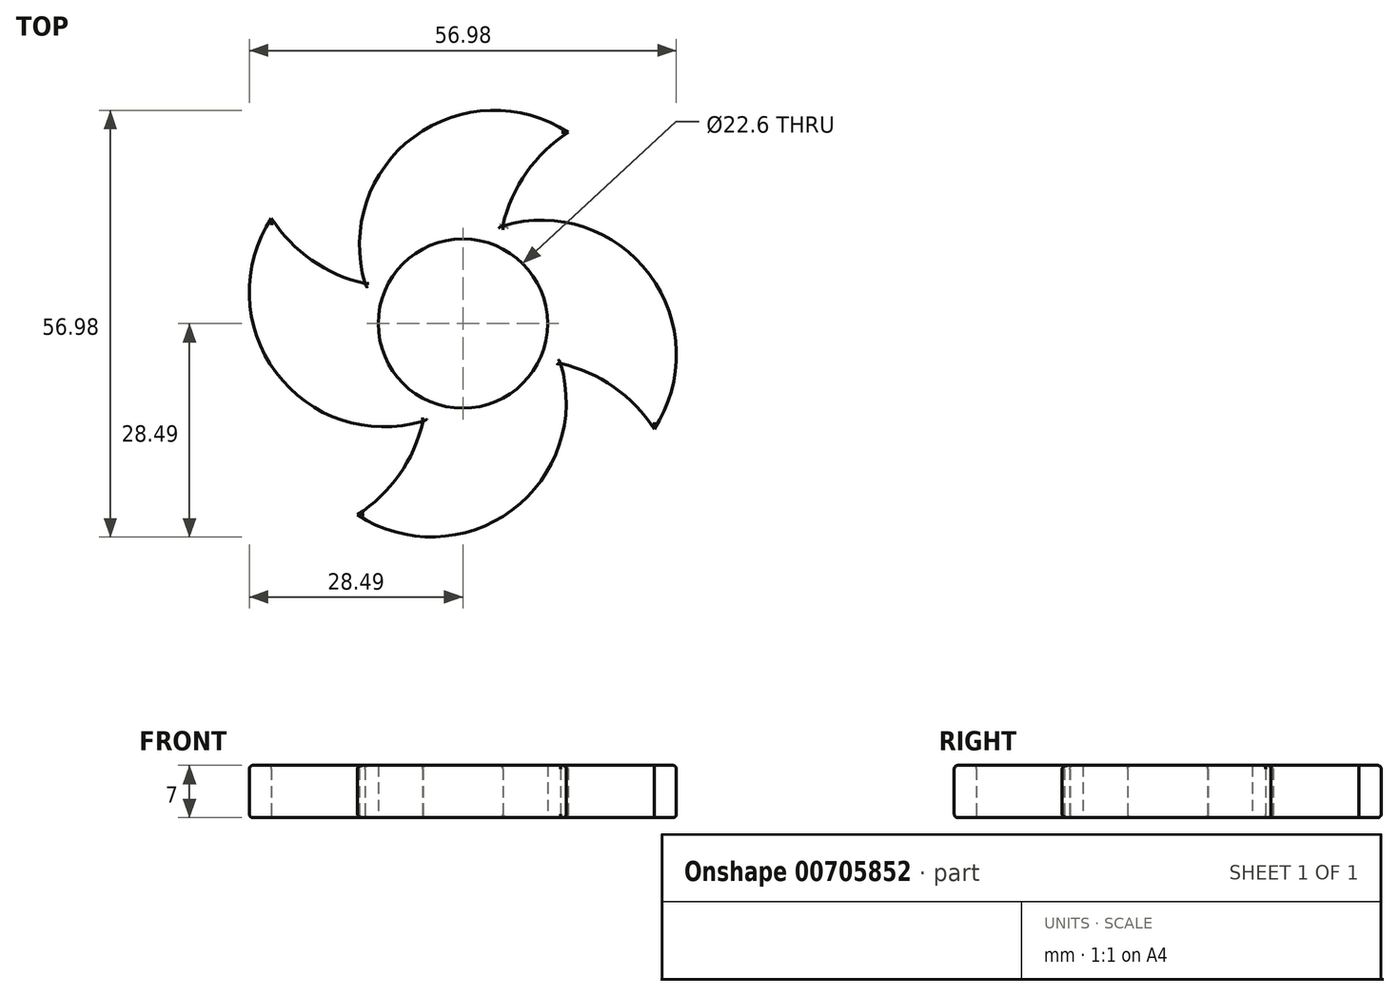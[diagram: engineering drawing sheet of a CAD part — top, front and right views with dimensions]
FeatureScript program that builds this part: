
annotation { "Feature Type Name" : "Feature", "Feature Type Description" : "" }
export const myFeature = defineFeature(function(context is Context, id is Id, definition is map)
    precondition{}
    {
        {
            var Q0;
            Q0=qCreatedBy(makeId("Top.planeOp"),FACE);
            var sketch = newSketch(context, id + "F0", { "sketchPlane" : qUnion([Q0])});
            skCircle(sketch, "E0", {"center": v(0, 0) * mm, "radius": 11.3 * mm});
            skCircle(sketch, "E1", {"center": v(0, 0) * mm, "radius": 14.12 * mm});
            skCircle(sketch, "E2", {"center": v(4.2, 10.5) * mm, "radius": 18 * mm});
            skCircle(sketch, "E3", {"center": v(24.85, 8.68) * mm, "radius": 20 * mm});
            skSolve(sketch);
        }
        {
            var Q0;
            {var subQ0=sQuery(id+"F0.wireOp",EDGE,"Av277wgP-tCuC-d8GK-UjtS-Sbt9RmJKMMHR");var subQ1=sQuery(id+"F0.wireOp",EDGE,"E1");var subQ2=makeQuery(id+"F0.imprint","INTERSECT",VERTEX,{"disambiguationData":[OD(0.0)],"derivedFrom":[subQ1,subQ0]});Q0=makeQuery(id+"F0.imprint","IMPRINT",FACE,{"disambiguationData":[TD([[makeQuery(id+"F0.imprint","IMPRINT",EDGE,{"disambiguationData":[TD([[subQ2,1.0]])],"derivedFrom":subQ1}),-1.0]])]});}
            var Q1;
            {var subQ0=sQuery(id+"F0.wireOp",EDGE,"Av277wgP-tCuC-d8GK-UjtS-Sbt9RmJKMMHR");var subQ1=sQuery(id+"F0.wireOp",EDGE,"E0");var subQ2=makeQuery(id+"F0.imprint","INTERSECT",VERTEX,{"disambiguationData":[OD(0.0)],"derivedFrom":[subQ1,subQ0]});Q1=makeQuery(id+"F0.imprint","IMPRINT",FACE,{"disambiguationData":[TD([[makeQuery(id+"F0.imprint","IMPRINT",EDGE,{"disambiguationData":[TD([[subQ2,-1.0]])],"derivedFrom":subQ1}),-1.0]])]});}
            var Q2;
            {var subQ0=sQuery(id+"F0.wireOp",EDGE,"Av277wgP-tCuC-d8GK-UjtS-Sbt9RmJKMMHR");var subQ1=sQuery(id+"F0.wireOp",EDGE,"E0");var subQ2=makeQuery(id+"F0.imprint","INTERSECT",VERTEX,{"disambiguationData":[OD(0.0)],"derivedFrom":[subQ1,subQ0]});Q2=makeQuery(id+"F0.imprint","IMPRINT",FACE,{"disambiguationData":[TD([[makeQuery(id+"F0.imprint","IMPRINT",EDGE,{"disambiguationData":[TD([[subQ2,1.0]])],"derivedFrom":subQ1}),-1.0]])]});}
            var Q3;
            {var subQ0=sQuery(id+"F0.wireOp",EDGE,"Av277wgP-tCuC-d8GK-UjtS-Sbt9RmJKMMHR");var subQ1=sQuery(id+"F0.wireOp",EDGE,"E0");var subQ2=makeQuery(id+"F0.imprint","INTERSECT",VERTEX,{"disambiguationData":[OD(1.0)],"derivedFrom":[subQ1,subQ0]});Q3=makeQuery(id+"F0.imprint","IMPRINT",FACE,{"disambiguationData":[TD([[makeQuery(id+"F0.imprint","IMPRINT",EDGE,{"disambiguationData":[TD([[subQ2,-1.0]])],"derivedFrom":subQ1}),-1.0]])]});}
            var Q4;
            {var subQ0=sQuery(id+"F0.wireOp",EDGE,"PTWYkS2m-cTii-Y78z-SZDI-GlTgDLrhLzSe");var subQ1=sQuery(id+"F0.wireOp",EDGE,"E0");var subQ2=makeQuery(id+"F0.imprint","INTERSECT",VERTEX,{"disambiguationData":[OD(0.0)],"derivedFrom":[subQ1,subQ0]});Q4=makeQuery(id+"F0.imprint","IMPRINT",FACE,{"disambiguationData":[TD([[makeQuery(id+"F0.imprint","IMPRINT",EDGE,{"disambiguationData":[TD([[subQ2,1.0]])],"derivedFrom":subQ1}),-1.0]])]});}
            var Q5;
            {var subQ0=sQuery(id+"F0.wireOp",EDGE,"LCob7wps-anE8-Zlfb-Umos-Snj1Pk7dvuzU");var subQ1=sQuery(id+"F0.wireOp",EDGE,"E0");var subQ2=makeQuery(id+"F0.imprint","INTERSECT",VERTEX,{"disambiguationData":[OD(0.0)],"derivedFrom":[subQ1,subQ0]});Q5=makeQuery(id+"F0.imprint","IMPRINT",FACE,{"disambiguationData":[TD([[makeQuery(id+"F0.imprint","IMPRINT",EDGE,{"disambiguationData":[TD([[subQ2,1.0]])],"derivedFrom":subQ1}),-1.0]])]});}
            var Q6;
            {var subQ0=sQuery(id+"F0.wireOp",EDGE,"LCob7wps-anE8-Zlfb-Umos-Snj1Pk7dvuzU");var subQ1=sQuery(id+"F0.wireOp",EDGE,"E0");var subQ2=makeQuery(id+"F0.imprint","INTERSECT",VERTEX,{"disambiguationData":[OD(0.0)],"derivedFrom":[subQ1,subQ0]});Q6=makeQuery(id+"F0.imprint","IMPRINT",FACE,{"disambiguationData":[TD([[makeQuery(id+"F0.imprint","IMPRINT",EDGE,{"disambiguationData":[TD([[subQ2,-1.0]])],"derivedFrom":subQ1}),-1.0]])]});}
            var Q7;
            {var subQ0=sQuery(id+"F0.wireOp",EDGE,"E2");var subQ1=sQuery(id+"F0.wireOp",EDGE,"E0");var subQ2=makeQuery(id+"F0.imprint","INTERSECT",VERTEX,{"disambiguationData":[OD(0.0)],"derivedFrom":[subQ1,subQ0]});Q7=makeQuery(id+"F0.imprint","IMPRINT",FACE,{"disambiguationData":[TD([[makeQuery(id+"F0.imprint","IMPRINT",EDGE,{"disambiguationData":[TD([[subQ2,-1.0]])],"derivedFrom":subQ1}),-1.0]])]});}
            var Q8;
            {var subQ0=sQuery(id+"F0.wireOp",EDGE,"LCob7wps-anE8-Zlfb-Umos-Snj1Pk7dvuzU");var subQ1=sQuery(id+"F0.wireOp",EDGE,"E0");var subQ2=makeQuery(id+"F0.imprint","INTERSECT",VERTEX,{"disambiguationData":[OD(1.0)],"derivedFrom":[subQ1,subQ0]});Q8=makeQuery(id+"F0.imprint","IMPRINT",FACE,{"disambiguationData":[TD([[makeQuery(id+"F0.imprint","IMPRINT",EDGE,{"disambiguationData":[TD([[subQ2,1.0]])],"derivedFrom":subQ1}),-1.0]])]});}
            var Q9;
            {var subQ0=sQuery(id+"F0.wireOp",EDGE,"E2");var subQ1=sQuery(id+"F0.wireOp",EDGE,"E1");var subQ2=makeQuery(id+"F0.imprint","INTERSECT",VERTEX,{"disambiguationData":[OD(0.0)],"derivedFrom":[subQ1,subQ0]});Q9=makeQuery(id+"F0.imprint","IMPRINT",FACE,{"disambiguationData":[TD([[makeQuery(id+"F0.imprint","IMPRINT",EDGE,{"disambiguationData":[TD([[subQ2,1.0]])],"derivedFrom":subQ1}),-1.0]])]});}
            var Q10;
            {var subQ0=sQuery(id+"F0.wireOp",EDGE,"E2");var subQ1=sQuery(id+"F0.wireOp",EDGE,"E0");var subQ2=makeQuery(id+"F0.imprint","INTERSECT",VERTEX,{"disambiguationData":[OD(0.0)],"derivedFrom":[subQ1,subQ0]});Q10=makeQuery(id+"F0.imprint","IMPRINT",FACE,{"disambiguationData":[TD([[makeQuery(id+"F0.imprint","IMPRINT",EDGE,{"disambiguationData":[TD([[subQ2,1.0]])],"derivedFrom":subQ1}),-1.0]])]});}
            var Q11;
            {var subQ0=sQuery(id+"F0.wireOp",EDGE,"E3");var subQ1=sQuery(id+"F0.wireOp",EDGE,"E0");var subQ2=makeQuery(id+"F0.imprint","INTERSECT",VERTEX,{"disambiguationData":[OD(0.0)],"derivedFrom":[subQ1,subQ0]});Q11=makeQuery(id+"F0.imprint","IMPRINT",FACE,{"disambiguationData":[TD([[makeQuery(id+"F0.imprint","IMPRINT",EDGE,{"disambiguationData":[TD([[subQ2,1.0]])],"derivedFrom":subQ1}),-1.0]])]});}
            var Q12;
            {var subQ0=sQuery(id+"F0.wireOp",EDGE,"E3");var subQ1=sQuery(id+"F0.wireOp",EDGE,"E0");var subQ2=makeQuery(id+"F0.imprint","INTERSECT",VERTEX,{"disambiguationData":[OD(1.0)],"derivedFrom":[subQ1,subQ0]});Q12=makeQuery(id+"F0.imprint","IMPRINT",FACE,{"disambiguationData":[TD([[makeQuery(id+"F0.imprint","IMPRINT",EDGE,{"disambiguationData":[TD([[subQ2,-1.0]])],"derivedFrom":subQ1}),-1.0]])]});}
            var Q13;
            {var subQ0=sQuery(id+"F0.wireOp",EDGE,"E3");var subQ1=sQuery(id+"F0.wireOp",EDGE,"E1");var subQ2=makeQuery(id+"F0.imprint","INTERSECT",VERTEX,{"disambiguationData":[OD(0.0)],"derivedFrom":[subQ1,subQ0]});Q13=makeQuery(id+"F0.imprint","IMPRINT",FACE,{"disambiguationData":[TD([[makeQuery(id+"F0.imprint","IMPRINT",EDGE,{"disambiguationData":[TD([[subQ2,-1.0]])],"derivedFrom":subQ1}),1.0]])]});}
            extrude(context, id + "F1", {"entities" : qUnion([Q0, Q1, Q2, Q3, Q4, Q5, Q6, Q7, Q8, Q9, Q10, Q11, Q12, Q13]), "endBound" : BoundingType.SYMMETRIC, "depth" : 7 * mm, "offsetDistance" : 25 * mm});
        }
        {
            var Q0;
            Q0=makeQuery(id+"F1.opExtrude","SWEPT_BODY",BODY,{"disambiguationData":[OSD([sQuery(id+"F0.wireOp",EDGE,"E0"),sQuery(id+"F0.wireOp",EDGE,"E1"),sQuery(id+"F0.wireOp",EDGE,"E2"),sQuery(id+"F0.wireOp",EDGE,"E3")])]});
            var Q1;
            Q1=makeQuery(id+"F1.opExtrude","SWEPT_FACE",FACE,{"disambiguationData":[OSD([sQuery(id+"F0.wireOp",EDGE,"E1")])]});
            circularPattern(context, id + "F2", {"entities" : qUnion([Q0]), "axis" : qUnion([Q1]), "angle" : 360 * degree, "instanceCount" : 4, "equalSpace" : true});
        }
        {
            var Q0;
            Q0=makeQuery(id+"F2.opPattern","COPY",BODY,{"derivedFrom":makeQuery(id+"F1.opExtrude","SWEPT_BODY",BODY,{"disambiguationData":[OSD([sQuery(id+"F0.wireOp",EDGE,"E0"),sQuery(id+"F0.wireOp",EDGE,"E1"),sQuery(id+"F0.wireOp",EDGE,"E2"),sQuery(id+"F0.wireOp",EDGE,"E3")])]}),"instanceName":"3"});
            var Q1;
            Q1=makeQuery(id+"F1.opExtrude","SWEPT_BODY",BODY,{"disambiguationData":[OSD([sQuery(id+"F0.wireOp",EDGE,"E0"),sQuery(id+"F0.wireOp",EDGE,"E1"),sQuery(id+"F0.wireOp",EDGE,"E2"),sQuery(id+"F0.wireOp",EDGE,"E3")])]});
            var Q2;
            Q2=makeQuery(id+"F2.opPattern","COPY",BODY,{"derivedFrom":makeQuery(id+"F1.opExtrude","SWEPT_BODY",BODY,{"disambiguationData":[OSD([sQuery(id+"F0.wireOp",EDGE,"E0"),sQuery(id+"F0.wireOp",EDGE,"E1"),sQuery(id+"F0.wireOp",EDGE,"E2"),sQuery(id+"F0.wireOp",EDGE,"E3")])]}),"instanceName":"1"});
            var Q3;
            Q3=makeQuery(id+"F2.opPattern","COPY",BODY,{"derivedFrom":makeQuery(id+"F1.opExtrude","SWEPT_BODY",BODY,{"disambiguationData":[OSD([sQuery(id+"F0.wireOp",EDGE,"E0"),sQuery(id+"F0.wireOp",EDGE,"E1"),sQuery(id+"F0.wireOp",EDGE,"E2"),sQuery(id+"F0.wireOp",EDGE,"E3")])]}),"instanceName":"2"});
            booleanBodies(context, id + "F3", {"operationType" : BooleanOperationType.UNION, "tools" : qUnion([Q0, Q1, Q2, Q3])});
        }
        {
            var Q0;
            Q0=makeQuery(id+"F2.opPattern","COPY",EDGE,{"derivedFrom":makeQuery(id+"F1.opExtrude","CAP_EDGE",EDGE,{"disambiguationData":[OSD([sQuery(id+"F0.wireOp",EDGE,"E3")])],"isStart":false}),"instanceName":"1"});
            var Q1;
            Q1=makeQuery(id+"F2.opPattern","COPY",EDGE,{"derivedFrom":makeQuery(id+"F1.opExtrude","CAP_EDGE",EDGE,{"disambiguationData":[OSD([sQuery(id+"F0.wireOp",EDGE,"E3")])],"isStart":true}),"instanceName":"1"});
            var Q2;
            Q2=makeQuery(id+"F2.opPattern","COPY",EDGE,{"derivedFrom":makeQuery(id+"F1.opExtrude","CAP_EDGE",EDGE,{"disambiguationData":[OSD([sQuery(id+"F0.wireOp",EDGE,"E3")])],"isStart":true}),"instanceName":"2"});
            var Q3;
            Q3=makeQuery(id+"F2.opPattern","COPY",EDGE,{"derivedFrom":makeQuery(id+"F1.opExtrude","CAP_EDGE",EDGE,{"disambiguationData":[OSD([sQuery(id+"F0.wireOp",EDGE,"E3")])],"isStart":false}),"instanceName":"2"});
            var Q4;
            Q4=makeQuery(id+"F2.opPattern","COPY",EDGE,{"derivedFrom":makeQuery(id+"F1.opExtrude","CAP_EDGE",EDGE,{"disambiguationData":[OSD([sQuery(id+"F0.wireOp",EDGE,"E3")])],"isStart":false}),"instanceName":"3"});
            var Q5;
            Q5=makeQuery(id+"F2.opPattern","COPY",EDGE,{"derivedFrom":makeQuery(id+"F1.opExtrude","CAP_EDGE",EDGE,{"disambiguationData":[OSD([sQuery(id+"F0.wireOp",EDGE,"E3")])],"isStart":true}),"instanceName":"3"});
            var Q6;
            Q6=makeQuery(id+"F1.opExtrude","CAP_EDGE",EDGE,{"disambiguationData":[OSD([sQuery(id+"F0.wireOp",EDGE,"E3")])],"isStart":false});
            var Q7;
            Q7=makeQuery(id+"F1.opExtrude","CAP_EDGE",EDGE,{"disambiguationData":[OSD([sQuery(id+"F0.wireOp",EDGE,"E3")])],"isStart":true});
            var Q8;
            Q8=makeQuery(id+"F2.opPattern","COPY",EDGE,{"derivedFrom":makeQuery(id+"F1.opExtrude","CAP_EDGE",EDGE,{"disambiguationData":[OSD([sQuery(id+"F0.wireOp",EDGE,"E2")])],"isStart":true}),"instanceName":"1"});
            var Q9;
            Q9=makeQuery(id+"F1.opExtrude","CAP_EDGE",EDGE,{"disambiguationData":[OSD([sQuery(id+"F0.wireOp",EDGE,"E2")])],"isStart":true});
            var Q10;
            Q10=makeQuery(id+"F1.opExtrude","CAP_EDGE",EDGE,{"disambiguationData":[OSD([sQuery(id+"F0.wireOp",EDGE,"E2")])],"isStart":false});
            var Q11;
            Q11=makeQuery(id+"F2.opPattern","COPY",EDGE,{"derivedFrom":makeQuery(id+"F1.opExtrude","CAP_EDGE",EDGE,{"disambiguationData":[OSD([sQuery(id+"F0.wireOp",EDGE,"E2")])],"isStart":false}),"instanceName":"1"});
            var Q12;
            Q12=makeQuery(id+"F2.opPattern","COPY",EDGE,{"derivedFrom":makeQuery(id+"F1.opExtrude","CAP_EDGE",EDGE,{"disambiguationData":[OSD([sQuery(id+"F0.wireOp",EDGE,"E2")])],"isStart":true}),"instanceName":"3"});
            var Q13;
            Q13=makeQuery(id+"F2.opPattern","COPY",EDGE,{"derivedFrom":makeQuery(id+"F1.opExtrude","CAP_EDGE",EDGE,{"disambiguationData":[OSD([sQuery(id+"F0.wireOp",EDGE,"E2")])],"isStart":false}),"instanceName":"3"});
            var Q14;
            Q14=makeQuery(id+"F2.opPattern","COPY",EDGE,{"derivedFrom":makeQuery(id+"F1.opExtrude","CAP_EDGE",EDGE,{"disambiguationData":[OSD([sQuery(id+"F0.wireOp",EDGE,"E2")])],"isStart":true}),"instanceName":"2"});
            var Q15;
            Q15=makeQuery(id+"F2.opPattern","COPY",EDGE,{"derivedFrom":makeQuery(id+"F1.opExtrude","CAP_EDGE",EDGE,{"disambiguationData":[OSD([sQuery(id+"F0.wireOp",EDGE,"E2")])],"isStart":false}),"instanceName":"2"});
            var Q16;
            {var subQ1=sQuery(id+"F0.wireOp",EDGE,"E2");var subQ2=sQuery(id+"F0.wireOp",EDGE,"E1");Q16=makeQuery(id+"F3.opBoolean","SPLIT",EDGE,{"disambiguationData":[TD([makeQuery(id+"F1.opExtrude","SWEPT_FACE",FACE,{"disambiguationData":[OSD([subQ1])]})])],"derivedFrom":makeQuery(id+"F2.opPattern","COPY",EDGE,{"derivedFrom":makeQuery(id+"F1.opExtrude","CAP_EDGE",EDGE,{"disambiguationData":[OSD([subQ2])],"isStart":false}),"instanceName":"3"})});}
            var Q17;
            {var subQ1=sQuery(id+"F0.wireOp",EDGE,"E2");var subQ2=sQuery(id+"F0.wireOp",EDGE,"E1");Q17=makeQuery(id+"F3.opBoolean","SPLIT",EDGE,{"disambiguationData":[TD([makeQuery(id+"F1.opExtrude","SWEPT_FACE",FACE,{"disambiguationData":[OSD([subQ1])]})])],"derivedFrom":makeQuery(id+"F2.opPattern","COPY",EDGE,{"derivedFrom":makeQuery(id+"F1.opExtrude","CAP_EDGE",EDGE,{"disambiguationData":[OSD([subQ2])],"isStart":true}),"instanceName":"3"})});}
            var Q18;
            {var subQ0=sQuery(id+"F0.wireOp",EDGE,"E3");var subQ2=sQuery(id+"F0.wireOp",EDGE,"E1");Q18=makeQuery(id+"F3.opBoolean","SPLIT",EDGE,{"disambiguationData":[TD([makeQuery(id+"F1.opExtrude","SWEPT_FACE",FACE,{"disambiguationData":[OSD([subQ0])]})])],"derivedFrom":makeQuery(id+"F2.opPattern","COPY",EDGE,{"derivedFrom":makeQuery(id+"F1.opExtrude","CAP_EDGE",EDGE,{"disambiguationData":[OSD([subQ2])],"isStart":false}),"instanceName":"3"})});}
            var Q19;
            {var subQ0=sQuery(id+"F0.wireOp",EDGE,"E3");var subQ2=sQuery(id+"F0.wireOp",EDGE,"E1");Q19=makeQuery(id+"F3.opBoolean","SPLIT",EDGE,{"disambiguationData":[TD([makeQuery(id+"F2.opPattern","COPY",FACE,{"derivedFrom":makeQuery(id+"F1.opExtrude","SWEPT_FACE",FACE,{"disambiguationData":[OSD([subQ0])]}),"instanceName":"1"})])],"derivedFrom":makeQuery(id+"F2.opPattern","COPY",EDGE,{"derivedFrom":makeQuery(id+"F1.opExtrude","CAP_EDGE",EDGE,{"disambiguationData":[OSD([subQ2])],"isStart":true}),"instanceName":"3"})});}
            var Q20;
            {var subQ0=sQuery(id+"F0.wireOp",EDGE,"E3");var subQ2=sQuery(id+"F0.wireOp",EDGE,"E1");Q20=makeQuery(id+"F3.opBoolean","SPLIT",EDGE,{"disambiguationData":[TD([makeQuery(id+"F2.opPattern","COPY",FACE,{"derivedFrom":makeQuery(id+"F1.opExtrude","SWEPT_FACE",FACE,{"disambiguationData":[OSD([subQ0])]}),"instanceName":"2"})])],"derivedFrom":makeQuery(id+"F2.opPattern","COPY",EDGE,{"derivedFrom":makeQuery(id+"F1.opExtrude","CAP_EDGE",EDGE,{"disambiguationData":[OSD([subQ2])],"isStart":true}),"instanceName":"3"})});}
            var Q21;
            {var subQ0=sQuery(id+"F0.wireOp",EDGE,"E3");var subQ2=sQuery(id+"F0.wireOp",EDGE,"E1");Q21=makeQuery(id+"F3.opBoolean","SPLIT",EDGE,{"disambiguationData":[TD([makeQuery(id+"F2.opPattern","COPY",FACE,{"derivedFrom":makeQuery(id+"F1.opExtrude","SWEPT_FACE",FACE,{"disambiguationData":[OSD([subQ0])]}),"instanceName":"2"})])],"derivedFrom":makeQuery(id+"F2.opPattern","COPY",EDGE,{"derivedFrom":makeQuery(id+"F1.opExtrude","CAP_EDGE",EDGE,{"disambiguationData":[OSD([subQ2])],"isStart":false}),"instanceName":"3"})});}
            var Q22;
            {var subQ0=sQuery(id+"F0.wireOp",EDGE,"E3");var subQ2=sQuery(id+"F0.wireOp",EDGE,"E1");Q22=makeQuery(id+"F3.opBoolean","SPLIT",EDGE,{"disambiguationData":[TD([makeQuery(id+"F2.opPattern","COPY",FACE,{"derivedFrom":makeQuery(id+"F1.opExtrude","SWEPT_FACE",FACE,{"disambiguationData":[OSD([subQ0])]}),"instanceName":"1"})])],"derivedFrom":makeQuery(id+"F2.opPattern","COPY",EDGE,{"derivedFrom":makeQuery(id+"F1.opExtrude","CAP_EDGE",EDGE,{"disambiguationData":[OSD([subQ2])],"isStart":false}),"instanceName":"3"})});}
            fillet(context, id + "F4", {"entities" : qUnion([Q0, Q1, Q2, Q3, Q4, Q5, Q6, Q7, Q8, Q9, Q10, Q11, Q12, Q13, Q14, Q15, Q16, Q17, Q18, Q19, Q20, Q21, Q22]), "radius" : 0.48 * mm, "tangentPropagation" : true, "allowEdgeOverflow" : false});
        }
    });
